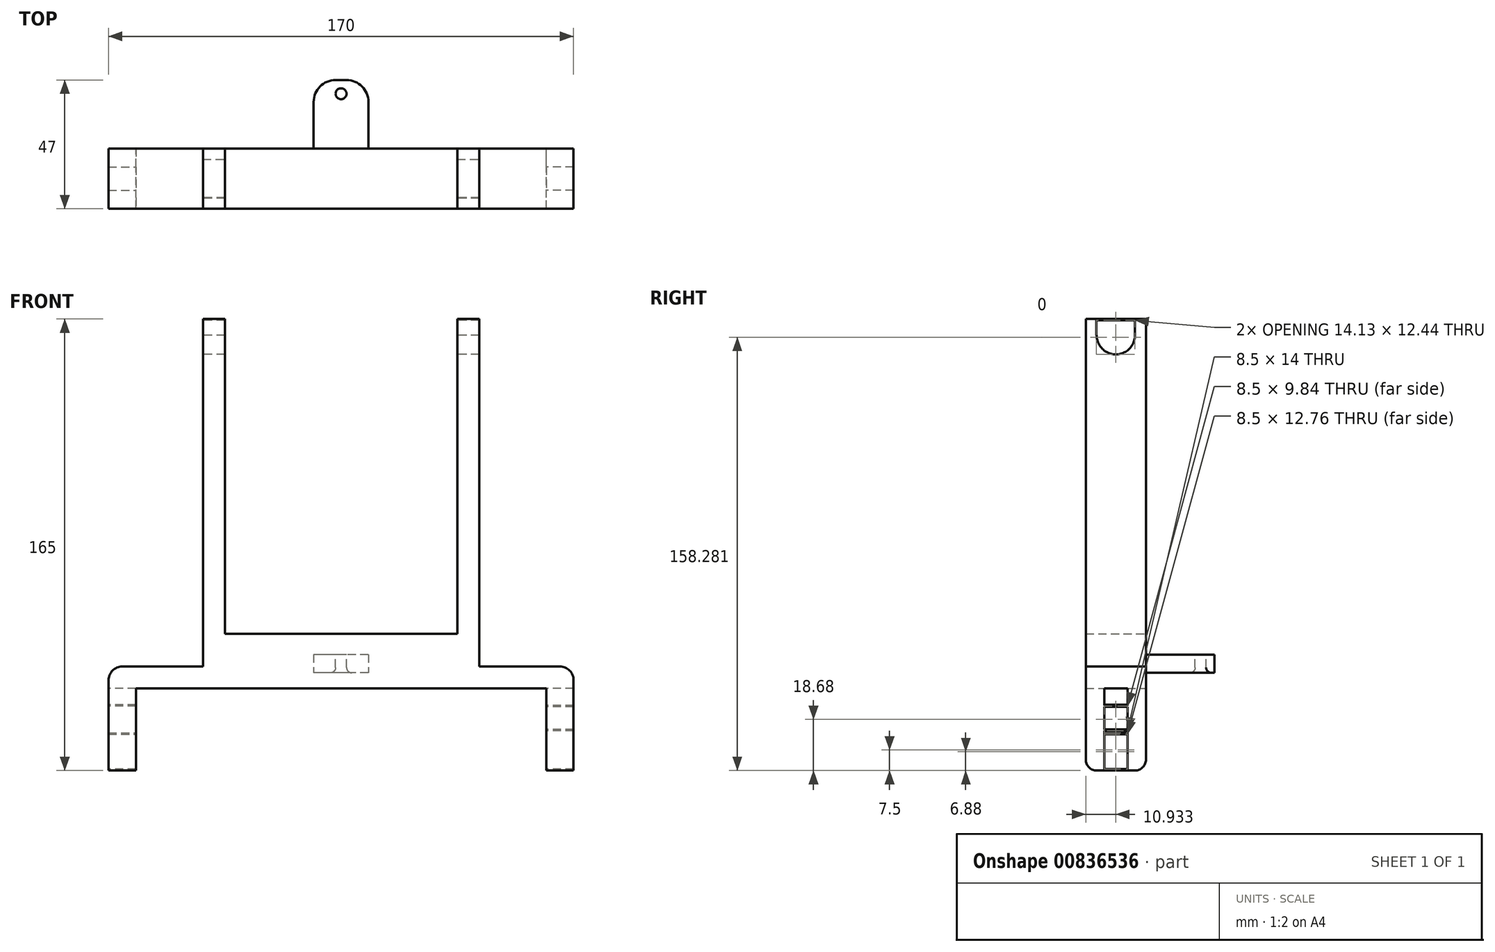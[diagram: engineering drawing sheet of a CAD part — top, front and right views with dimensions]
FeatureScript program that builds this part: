
annotation { "Feature Type Name" : "Feature", "Feature Type Description" : "" }
export const myFeature = defineFeature(function(context is Context, id is Id, definition is map)
    precondition{}
    {
        {
            var Q0;
            Q0=qCreatedBy(makeId("Front.planeOp"),FACE);
            var sketch = newSketch(context, id + "F0", { "sketchPlane" : qUnion([Q0])});
            skLineSegment(sketch, "E0", {"start": v(-42.5, 115) * mm, "end": v(-42.5, 0) * mm});
            skLineSegment(sketch, "E1", {"start": v(-42.5, 0) * mm, "end": v(42.5, 0) * mm});
            skLineSegment(sketch, "E2", {"start": v(42.5, 0) * mm, "end": v(42.5, 115) * mm});
            skLineSegment(sketch, "E3", {"start": v(42.5, 115) * mm, "end": v(50.5, 115) * mm});
            skLineSegment(sketch, "E4", {"start": v(50.5, 115) * mm, "end": v(50.5, -12) * mm});
            skLineSegment(sketch, "E5", {"start": v(50.5, -12) * mm, "end": v(-50.5, -12) * mm});
            skLineSegment(sketch, "E6", {"start": v(-50.5, -12) * mm, "end": v(-50.5, 115) * mm});
            skLineSegment(sketch, "E7", {"start": v(-50.5, 115) * mm, "end": v(-42.5, 115) * mm});
            skLineSegment(sketch, "E8", {"start": v(-50.5, 115) * mm, "end": v(50.02, 115) * mm, "construction": true});
            skLineSegment(sketch, "E9", {"start": v(0, -12) * mm, "end": v(-85, -12) * mm});
            skLineSegment(sketch, "E10", {"start": v(-85, -12) * mm, "end": v(-85, -50) * mm});
            skLineSegment(sketch, "E11", {"start": v(-85, -50) * mm, "end": v(-75, -50) * mm});
            skLineSegment(sketch, "E12", {"start": v(-75, -50) * mm, "end": v(-75, -20) * mm});
            skLineSegment(sketch, "E13", {"start": v(-75, -20) * mm, "end": v(75, -20) * mm});
            skLineSegment(sketch, "E14", {"start": v(75, -20) * mm, "end": v(75, -50) * mm});
            skLineSegment(sketch, "E15", {"start": v(75, -50) * mm, "end": v(85, -50) * mm});
            skLineSegment(sketch, "E16", {"start": v(85, -50) * mm, "end": v(85, -12) * mm});
            skLineSegment(sketch, "E17", {"start": v(85, -12) * mm, "end": v(50.5, -12) * mm});
            skSolve(sketch);
        }
        {
            var Q0;
            Q0 = qSketchRegion(id + "F0", true);
            extrude(context, id + "F1", {"entities" : qUnion([Q0]), "depth" : 22 * mm, "offsetDistance" : 25 * mm});
        }
        {
            var Q0;
            Q0=makeQuery(id+"F1.opExtrude","SWEPT_EDGE",EDGE,{"disambiguationData":[OSD([sQuery(id+"F0.wireOp",EDGE,"E9"),sQuery(id+"F0.wireOp",EDGE,"E10")])]});
            var Q1;
            Q1=makeQuery(id+"F1.opExtrude","SWEPT_EDGE",EDGE,{"disambiguationData":[OSD([sQuery(id+"F0.wireOp",EDGE,"E16"),sQuery(id+"F0.wireOp",EDGE,"E17")])]});
            fillet(context, id + "F2", {"entities" : qUnion([Q0, Q1]), "radius" : 5 * mm, "tangentPropagation" : true, "allowEdgeOverflow" : false});
        }
        {
            var Q0;
            Q0=makeQuery(id+"F1.opExtrude","SWEPT_FACE",FACE,{"disambiguationData":[OSD([sQuery(id+"F0.wireOp",EDGE,"E6")])]});
            var sketch = newSketch(context, id + "F3", { "sketchPlane" : qUnion([Q0])});
            skCircle(sketch, "E18", {"center": v(11, 109.06) * mm, "radius": 7 * mm});
            skPoint(sketch, "E18.centerSnap0", {"position": v(11, 115) * mm});
            skLineSegment(sketch, "E19.bottom", {"start": v(4, 109.09) * mm, "end": v(18.13, 109.09) * mm});
            skLineSegment(sketch, "E19.top", {"start": v(4, 118.56) * mm, "end": v(18.13, 118.56) * mm});
            skLineSegment(sketch, "E19.left", {"start": v(4, 109.09) * mm, "end": v(4, 118.56) * mm});
            skLineSegment(sketch, "E19.right", {"start": v(18.13, 109.09) * mm, "end": v(18.13, 118.56) * mm});
            skSolve(sketch);
        }
        {
            var Q0;
            {var subQ1=sQuery(id+"F3.wireOp",EDGE,"E19.top");Q0=makeQuery(id+"F3.imprint","IMPRINT",FACE,{"disambiguationData":[TD([[makeQuery(id+"F3.imprint","IMPRINT",EDGE,{"derivedFrom":subQ1}),-1.0]])]});}
            var Q1;
            {var subQ0=sQuery(id+"F3.wireOp",EDGE,"E19.bottom");var subQ1=sQuery(id+"F3.wireOp",EDGE,"E18");var subQ2=makeQuery(id+"F3.imprint","INTERSECT",VERTEX,{"derivedFrom":[subQ1,subQ0]});Q1=makeQuery(id+"F3.imprint","IMPRINT",FACE,{"disambiguationData":[TD([[makeQuery(id+"F3.imprint","IMPRINT",EDGE,{"disambiguationData":[TD([[subQ2,-1.0]])],"derivedFrom":subQ1}),1.0]])]});}
            var Q2;
            {var subQ0=sQuery(id+"F3.wireOp",EDGE,"E19.bottom");var subQ1=sQuery(id+"F3.wireOp",EDGE,"E18");var subQ3=makeQuery(id+"F3.imprint","INTERSECT",VERTEX,{"derivedFrom":[subQ1,subQ0]});Q2=makeQuery(id+"F3.imprint","IMPRINT",FACE,{"disambiguationData":[TD([[makeQuery(id+"F3.imprint","IMPRINT",EDGE,{"disambiguationData":[TD([[subQ3,1.0]])],"derivedFrom":subQ1}),1.0]])]});}
            var Q3;
            {var subQ0=sQuery(id+"F3.wireOp",EDGE,"E19.bottom");var subQ5=sQuery(id+"F3.wireOp",EDGE,"E19.right");var subQ6=makeQuery(id+"F3.imprint","INTERSECT",VERTEX,{"derivedFrom":[subQ0,subQ5]});Q3=makeQuery(id+"F3.imprint","IMPRINT",FACE,{"disambiguationData":[TD([[makeQuery(id+"F3.imprint","IMPRINT",EDGE,{"disambiguationData":[TD([[subQ6,1.0]])],"derivedFrom":subQ0}),1.0]])]});}
            var Q4;
            {var subQ0=sQuery(id+"F3.wireOp",EDGE,"E19.left");var subQ1=sQuery(id+"F3.wireOp",EDGE,"E18");var subQ2=makeQuery(id+"F3.imprint","INTERSECT",VERTEX,{"derivedFrom":[subQ1,sQuery(id+"F3.wireOp",EDGE,"E19.bottom"),subQ0]});Q4=makeQuery(id+"F3.imprint","IMPRINT",FACE,{"disambiguationData":[TD([[makeQuery(id+"F3.imprint","IMPRINT",EDGE,{"disambiguationData":[TD([[subQ2,1.0]])],"derivedFrom":subQ1}),-1.0]])]});}
            extrude(context, id + "F4", {"entities" : qUnion([Q0, Q1, Q2, Q3, Q4]), "operationType" : NewBodyOperationType.REMOVE, "oppositeDirection" : true, "depth" : 180 * mm, "offsetDistance" : 25 * mm});
        }
        {
            var Q0;
            {var subQ0=sQuery(id+"F3.wireOp",EDGE,"E19.left");Q0=makeQuery(id+"F4.boolean.opBoolean","COPY",FACE,{"disambiguationData":[TD([makeQuery(id+"F1.opExtrude","SWEPT_FACE",FACE,{"disambiguationData":[OSD([sQuery(id+"F0.wireOp",EDGE,"E0")])]})])],"derivedFrom":makeQuery(id+"F4.opExtrude","SWEPT_FACE",FACE,{"disambiguationData":[OSD([subQ0])]})});}
            var sketch = newSketch(context, id + "F5", { "sketchPlane" : qUnion([Q0])});
            skLineSegment(sketch, "E20.bottom", {"start": v(-50.5, 115) * mm, "end": v(-42.5, 115) * mm});
            skLineSegment(sketch, "E20.top", {"start": v(-50.5, 114.5) * mm, "end": v(-42.5, 114.5) * mm});
            skLineSegment(sketch, "E20.left", {"start": v(-50.5, 115) * mm, "end": v(-50.5, 114.5) * mm});
            skLineSegment(sketch, "E20.right", {"start": v(-42.5, 115) * mm, "end": v(-42.5, 114.5) * mm});
            skSolve(sketch);
        }
        {
            var Q0;
            Q0 = qSketchRegion(id + "F5", true);
            extrude(context, id + "F6", {"entities" : qUnion([Q0]), "operationType" : NewBodyOperationType.ADD, "depth" : 15 * mm, "offsetDistance" : 25 * mm});
        }
        {
            var Q0;
            {var subQ0=sQuery(id+"F3.wireOp",EDGE,"E19.left");Q0=makeQuery(id+"F4.boolean.opBoolean","COPY",FACE,{"disambiguationData":[TD([makeQuery(id+"F1.opExtrude","SWEPT_FACE",FACE,{"disambiguationData":[OSD([sQuery(id+"F0.wireOp",EDGE,"E2")])]})])],"derivedFrom":makeQuery(id+"F4.opExtrude","SWEPT_FACE",FACE,{"disambiguationData":[OSD([subQ0])]})});}
            var sketch = newSketch(context, id + "F7", { "sketchPlane" : qUnion([Q0])});
            skLineSegment(sketch, "E21.bottom", {"start": v(42.5, 115) * mm, "end": v(50.5, 115) * mm});
            skLineSegment(sketch, "E21.top", {"start": v(42.5, 114.5) * mm, "end": v(50.5, 114.5) * mm});
            skLineSegment(sketch, "E21.left", {"start": v(42.5, 115) * mm, "end": v(42.5, 114.5) * mm});
            skLineSegment(sketch, "E21.right", {"start": v(50.5, 115) * mm, "end": v(50.5, 114.5) * mm});
            skSolve(sketch);
        }
        {
            var Q0;
            Q0 = qSketchRegion(id + "F7", true);
            extrude(context, id + "F8", {"entities" : qUnion([Q0]), "operationType" : NewBodyOperationType.ADD, "depth" : 15 * mm, "offsetDistance" : 25 * mm});
        }
        {
            var Q0;
            Q0=makeQuery(id+"F1.opExtrude","CAP_EDGE",EDGE,{"disambiguationData":[OSD([sQuery(id+"F0.wireOp",EDGE,"E11")])],"isStart":false});
            var Q1;
            Q1=makeQuery(id+"F1.opExtrude","CAP_EDGE",EDGE,{"disambiguationData":[OSD([sQuery(id+"F0.wireOp",EDGE,"E11")])],"isStart":true});
            var Q2;
            Q2=makeQuery(id+"F1.opExtrude","CAP_EDGE",EDGE,{"disambiguationData":[OSD([sQuery(id+"F0.wireOp",EDGE,"E15")])],"isStart":false});
            var Q3;
            Q3=makeQuery(id+"F1.opExtrude","CAP_EDGE",EDGE,{"disambiguationData":[OSD([sQuery(id+"F0.wireOp",EDGE,"E15")])],"isStart":true});
            fillet(context, id + "F9", {"entities" : qUnion([Q0, Q1, Q2, Q3]), "radius" : 4 * mm, "tangentPropagation" : true, "allowEdgeOverflow" : false});
        }
        {
            var Q0;
            Q0=makeQuery(id+"F1.opExtrude","SWEPT_FACE",FACE,{"disambiguationData":[OSD([sQuery(id+"F0.wireOp",EDGE,"E10")])]});
            var sketch = newSketch(context, id + "F10", { "sketchPlane" : qUnion([Q0])});
            skLineSegment(sketch, "E22.bottom", {"start": v(6.73, -50) * mm, "end": v(15.23, -50) * mm});
            skLineSegment(sketch, "E22.top", {"start": v(6.73, -20) * mm, "end": v(15.23, -20) * mm});
            skLineSegment(sketch, "E22.left", {"start": v(6.73, -50) * mm, "end": v(6.73, -20) * mm});
            skLineSegment(sketch, "E22.right", {"start": v(15.23, -50) * mm, "end": v(15.23, -20) * mm});
            skSolve(sketch);
        }
        {
            var Q0;
            Q0 = qSketchRegion(id + "F10", true);
            extrude(context, id + "F11", {"entities" : qUnion([Q0]), "operationType" : NewBodyOperationType.REMOVE, "oppositeDirection" : true, "depth" : 195 * mm, "offsetDistance" : 25 * mm});
        }
        {
            var Q0;
            Q0=makeQuery(id+"F1.opExtrude","CAP_FACE",FACE,{"disambiguationData":[OSD([sQuery(id+"F0.wireOp",EDGE,"E0"),sQuery(id+"F0.wireOp",EDGE,"E1"),sQuery(id+"F0.wireOp",EDGE,"E2"),sQuery(id+"F0.wireOp",EDGE,"E3"),sQuery(id+"F0.wireOp",EDGE,"E4"),sQuery(id+"F0.wireOp",EDGE,"E6"),sQuery(id+"F0.wireOp",EDGE,"E7"),sQuery(id+"F0.wireOp",EDGE,"E9"),sQuery(id+"F0.wireOp",EDGE,"E10"),sQuery(id+"F0.wireOp",EDGE,"E11"),sQuery(id+"F0.wireOp",EDGE,"E12"),sQuery(id+"F0.wireOp",EDGE,"E13"),sQuery(id+"F0.wireOp",EDGE,"E14"),sQuery(id+"F0.wireOp",EDGE,"E15"),sQuery(id+"F0.wireOp",EDGE,"E16"),sQuery(id+"F0.wireOp",EDGE,"E17")])],"isStart":true});
            var sketch = newSketch(context, id + "F12", { "sketchPlane" : qUnion([Q0])});
            skLineSegment(sketch, "E23", {"start": v(-42.5, -12) * mm, "end": v(39.68, -12) * mm, "construction": true});
            skLineSegment(sketch, "E24.bottom", {"start": v(-10, -7.63) * mm, "end": v(10, -7.63) * mm});
            skLineSegment(sketch, "E24.top", {"start": v(-10, -14.3) * mm, "end": v(10, -14.3) * mm});
            skLineSegment(sketch, "E24.left", {"start": v(-10, -7.63) * mm, "end": v(-10, -14.3) * mm});
            skLineSegment(sketch, "E24.right", {"start": v(10, -7.63) * mm, "end": v(10, -14.3) * mm});
            skSolve(sketch);
        }
        {
            var Q0;
            Q0=makeQuery(id+"F12.imprint","IMPRINT",FACE,{"disambiguationData":[TD([[makeQuery(id+"F12.imprint","IMPRINT",EDGE,{"derivedFrom":sQuery(id+"F12.wireOp",EDGE,"E24.bottom")}),-1.0]])]});
            extrude(context, id + "F13", {"entities" : qUnion([Q0]), "operationType" : NewBodyOperationType.ADD, "depth" : 25 * mm, "offsetDistance" : 25 * mm});
        }
        {
            var Q0;
            Q0=makeQuery(id+"F13.opExtrude","CAP_EDGE",EDGE,{"disambiguationData":[OSD([sQuery(id+"F12.wireOp",EDGE,"E24.left")])],"isStart":false});
            var Q1;
            Q1=makeQuery(id+"F13.opExtrude","CAP_EDGE",EDGE,{"disambiguationData":[OSD([sQuery(id+"F12.wireOp",EDGE,"E24.right")])],"isStart":false});
            fillet(context, id + "F14", {"entities" : qUnion([Q0, Q1]), "radius" : 8 * mm, "tangentPropagation" : true, "allowEdgeOverflow" : false});
        }
        {
            var Q0;
            Q0=makeQuery(id+"F13.opExtrude","SWEPT_FACE",FACE,{"disambiguationData":[OSD([sQuery(id+"F12.wireOp",EDGE,"E24.bottom")])]});
            var sketch = newSketch(context, id + "F15", { "sketchPlane" : qUnion([Q0])});
            skCircle(sketch, "E25", {"center": v(0, 20) * mm, "radius": 2 * mm});
            skSolve(sketch);
        }
        {
            var Q0;
            Q0 = qSketchRegion(id + "F15", true);
            extrude(context, id + "F16", {"entities" : qUnion([Q0]), "operationType" : NewBodyOperationType.REMOVE, "oppositeDirection" : true, "depth" : 25 * mm, "offsetDistance" : 25 * mm});
        }
        {
            var Q0;
            Q0=makeQuery(id+"F16.boolean.opBoolean","COPY",EDGE,{"derivedFrom":makeQuery(id+"F16.opExtrude","CAP_EDGE",EDGE,{"disambiguationData":[OSD([sQuery(id+"F15.wireOp",EDGE,"E25")])],"isStart":true})});
            var Q1;
            Q1=makeQuery(id+"F16.boolean.opBoolean","INTERSECT",EDGE,{"derivedFrom":[makeQuery(id+"F13.opExtrude","SWEPT_FACE",FACE,{"disambiguationData":[OSD([sQuery(id+"F12.wireOp",EDGE,"E24.top")])]}),makeQuery(id+"F16.opExtrude","SWEPT_FACE",FACE,{"disambiguationData":[OSD([sQuery(id+"F15.wireOp",EDGE,"E25")])]})]});
            fillet(context, id + "F17", {"entities" : qUnion([Q0, Q1]), "radius" : 2 * mm, "tangentPropagation" : true, "allowEdgeOverflow" : false});
        }
        {
            var Q0;
            Q0=makeQuery(id+"F11.boolean.opBoolean","COPY",FACE,{"disambiguationData":[TD([makeQuery(id+"F1.opExtrude","SWEPT_FACE",FACE,{"disambiguationData":[OSD([sQuery(id+"F0.wireOp",EDGE,"E14")])]})])],"derivedFrom":makeQuery(id+"F11.opExtrude","SWEPT_FACE",FACE,{"disambiguationData":[OSD([sQuery(id+"F10.wireOp",EDGE,"E22.right")])]})});
            var sketch = newSketch(context, id + "F18", { "sketchPlane" : qUnion([Q0])});
            skLineSegment(sketch, "E26.bottom", {"start": v(-85, -50) * mm, "end": v(-75, -50) * mm});
            skLineSegment(sketch, "E26.top", {"start": v(-85, -49.5) * mm, "end": v(-75, -49.5) * mm});
            skLineSegment(sketch, "E26.left", {"start": v(-85, -50) * mm, "end": v(-85, -49.5) * mm});
            skLineSegment(sketch, "E26.right", {"start": v(-75, -50) * mm, "end": v(-75, -49.5) * mm});
            skLineSegment(sketch, "E27.bottom", {"start": v(-85, -26.15) * mm, "end": v(-75, -26.15) * mm});
            skLineSegment(sketch, "E27.top", {"start": v(-85, -26.65) * mm, "end": v(-75, -26.65) * mm});
            skLineSegment(sketch, "E27.left", {"start": v(-85, -26.15) * mm, "end": v(-85, -26.65) * mm});
            skLineSegment(sketch, "E27.right", {"start": v(-75, -26.15) * mm, "end": v(-75, -26.65) * mm});
            skLineSegment(sketch, "E28.bottom", {"start": v(-85, -35) * mm, "end": v(-75, -35) * mm});
            skLineSegment(sketch, "E28.top", {"start": v(-85, -35.5) * mm, "end": v(-75, -35.5) * mm});
            skLineSegment(sketch, "E28.left", {"start": v(-85, -35) * mm, "end": v(-85, -35.5) * mm});
            skLineSegment(sketch, "E28.right", {"start": v(-75, -35) * mm, "end": v(-75, -35.5) * mm});
            skSolve(sketch);
        }
        {
            var Q0;
            Q0=makeQuery(id+"F18.imprint","IMPRINT",FACE,{"disambiguationData":[TD([[makeQuery(id+"F18.imprint","IMPRINT",EDGE,{"derivedFrom":sQuery(id+"F18.wireOp",EDGE,"E27.bottom")}),-1.0]])]});
            var Q1;
            Q1=makeQuery(id+"F18.imprint","IMPRINT",FACE,{"disambiguationData":[TD([[makeQuery(id+"F18.imprint","IMPRINT",EDGE,{"derivedFrom":sQuery(id+"F18.wireOp",EDGE,"E26.bottom")}),1.0]])]});
            var Q2;
            Q2=makeQuery(id+"F18.imprint","IMPRINT",FACE,{"disambiguationData":[TD([[makeQuery(id+"F18.imprint","IMPRINT",EDGE,{"derivedFrom":sQuery(id+"F18.wireOp",EDGE,"E28.bottom")}),-1.0]])]});
            extrude(context, id + "F19", {"entities" : qUnion([Q0, Q1, Q2]), "operationType" : NewBodyOperationType.ADD, "depth" : 10 * mm, "offsetDistance" : 25 * mm});
        }
        {
            var Q0;
            Q0=makeQuery(id+"F11.boolean.opBoolean","COPY",FACE,{"disambiguationData":[TD([makeQuery(id+"F1.opExtrude","SWEPT_FACE",FACE,{"disambiguationData":[OSD([sQuery(id+"F0.wireOp",EDGE,"E10")])]})])],"derivedFrom":makeQuery(id+"F11.opExtrude","SWEPT_FACE",FACE,{"disambiguationData":[OSD([sQuery(id+"F10.wireOp",EDGE,"E22.right")])]})});
            var sketch = newSketch(context, id + "F20", { "sketchPlane" : qUnion([Q0])});
            skLineSegment(sketch, "E29.bottom", {"start": v(75, -50) * mm, "end": v(85, -50) * mm});
            skLineSegment(sketch, "E29.top", {"start": v(75, -49.5) * mm, "end": v(85, -49.5) * mm});
            skLineSegment(sketch, "E29.left", {"start": v(75, -50) * mm, "end": v(75, -49.5) * mm});
            skLineSegment(sketch, "E29.right", {"start": v(85, -50) * mm, "end": v(85, -49.5) * mm});
            skLineSegment(sketch, "E30.bottom", {"start": v(75, -25.9) * mm, "end": v(85, -25.9) * mm});
            skLineSegment(sketch, "E30.top", {"start": v(75, -26.4) * mm, "end": v(85, -26.4) * mm});
            skLineSegment(sketch, "E30.left", {"start": v(75, -25.9) * mm, "end": v(75, -26.4) * mm});
            skLineSegment(sketch, "E30.right", {"start": v(85, -25.9) * mm, "end": v(85, -26.4) * mm});
            skLineSegment(sketch, "E31.bottom", {"start": v(85, -36.24) * mm, "end": v(75, -36.24) * mm});
            skLineSegment(sketch, "E31.top", {"start": v(85, -36.74) * mm, "end": v(75, -36.74) * mm});
            skLineSegment(sketch, "E31.left", {"start": v(85, -36.24) * mm, "end": v(85, -36.74) * mm});
            skLineSegment(sketch, "E31.right", {"start": v(75, -36.24) * mm, "end": v(75, -36.74) * mm});
            skSolve(sketch);
        }
        {
            var Q0;
            Q0=makeQuery(id+"F20.imprint","IMPRINT",FACE,{"disambiguationData":[TD([[makeQuery(id+"F20.imprint","IMPRINT",EDGE,{"derivedFrom":sQuery(id+"F20.wireOp",EDGE,"E30.bottom")}),-1.0]])]});
            var Q1;
            Q1=makeQuery(id+"F20.imprint","IMPRINT",FACE,{"disambiguationData":[TD([[makeQuery(id+"F20.imprint","IMPRINT",EDGE,{"derivedFrom":sQuery(id+"F20.wireOp",EDGE,"E29.bottom")}),1.0]])]});
            var Q2;
            Q2=makeQuery(id+"F20.imprint","IMPRINT",FACE,{"disambiguationData":[TD([[makeQuery(id+"F20.imprint","IMPRINT",EDGE,{"derivedFrom":sQuery(id+"F20.wireOp",EDGE,"E31.bottom")}),1.0]])]});
            extrude(context, id + "F21", {"entities" : qUnion([Q0, Q1, Q2]), "operationType" : NewBodyOperationType.ADD, "depth" : 9 * mm, "offsetDistance" : 25 * mm});
        }
    });
